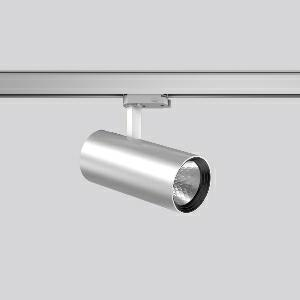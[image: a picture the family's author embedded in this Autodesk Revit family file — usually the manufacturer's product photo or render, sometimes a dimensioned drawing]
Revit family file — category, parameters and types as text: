
# Revit family: deecos_s_mini_742196_004_1_76_0237
name_source: partatom
category: Lighting Fixtures
units: mm (PartAtom-declared; Revit-internal decimal feet)

## family parameters
Cut with Voids When Loaded = No
Host = Face
Light Source = No
Part Type = Normal
Room Calculation Point = No
Round Connector Dimension = Use Diameter
Shared = No

## types (1)
- DEECOS S mini (1 x LED Modul 940, 2600 lm, 4000)
    Apparent Load = 20 VA
    Approval mark = CE
    CIE Flux Codes = 99 100 100 100 100
    Color Rendering = 92
    Color Temperature = 4000
    Default Elevation = 1800 mm
    Description = Series: DEECOS S mini
LED surface-mounted projector in modern design with no visible cooling ribs. Housing: die-cast aluminium, powder-coated. Rotation range: 356°. Swivel range: 90°. Black plastic ring and recessed LED to prevent glare from the side. Optical assembly with reflector made of MIRO-Silver with 98% total light reflection for outstanding efficiency - can be changed without tools. Best colour rendering index Ra>90. With adapter for RZB 3-circuit DALI tracks. Suitable for Track on ceiling, Wall track. High quality converter without flickering and stroboscopic effect. The following accessories can be mounted without use of tools: interchangeable lenses, decorative glasses, honeycomb louvre, clear and frosted diffusers, white interchangeable plastic ring. 
Colour: silver
Diameter: 87 mm
Height: 214 mm
Lamp: LED
Socket: without socket
Colour temperature: 4000K
Colour rendering index (CRI): 92
System power: 20 W
Rated luminous flux: 2600 lm
Luminous efficiency: 130 lm/W
Control gear: Converter, dimmable, DALI
Protection class: I
Type of protection: IP 20
    Height = 214 mm
    Lamp = 1 x LED Modul 940
    Lamp Light Flux = 2600 lm
    Lamp count = 1
    Length = 87 mm
    Lifetime = 50000 h
    Luminous efficacy = 130 lm/W
    Manufacturer = RZB
    ModVariant = No
    Model = 742196.004.1.76
    Mounting Place = Ceiling
    Mounting Type = Rail mounted
    Number of Poles = 1
    OnlyDefault = Yes
    Power Factor = 1
    Product Name = DEECOS S mini
    Product group = Track mounted projectors
    ProductGroupID = 301
    Protection Class = Protection class I
    Protection Degree = IP 20
    RLX_Detail_Level = 1
    RLX_Emergency_Light_Flux = 0 lm
    RLX_Emergency_Type = 0
    RLX_Emergency_Type_DB = No
    RlxData = <blob elided: 37333 chars, md5=17079d0b>
    Socket = socket
    Standby Power = 0 W
    System Light Flux = 2600 lm
    System Power = 20 W
    Type Comments = Product without accessories
    Type Image = 741926.004.jpg
    URL = http://relux.com
    VarID = ---
    Voltage = 230 V
    Voltage Range = 220-240 V
    Weight = 0.00 kg
    Width = 0 mm  [stored 0 ft]

note: [stored X ft] marks values corroborated as IEEE doubles in the binary element streams (Revit-internal decimal feet)

## geometry (parser evidence)
native form markers: Blend x4, Sweep x10
no freeform markers — native parametric forms only
